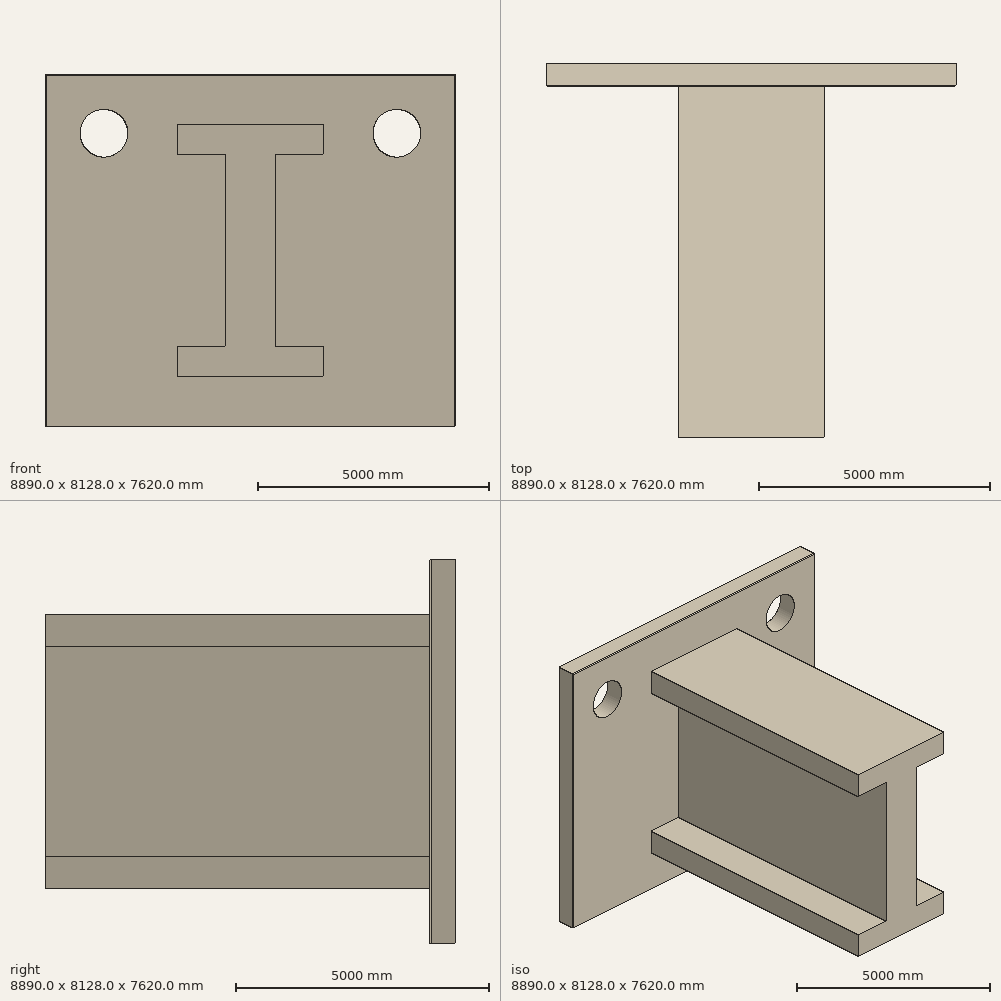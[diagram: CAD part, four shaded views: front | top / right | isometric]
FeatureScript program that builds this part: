
annotation { "Feature Type Name" : "Feature", "Feature Type Description" : "" }
export const myFeature = defineFeature(function(context is Context, id is Id, definition is map)
    precondition{}
    {
        {
            var Q0;
            Q0=qCreatedBy(makeId("Front.planeOp"),FACE);
            var sketch = newSketch(context, id + "F0", { "sketchPlane" : qUnion([Q0])});
            skLineSegment(sketch, "E0.bottom", {"start": v(-4445, 3810) * mm, "end": v(4445, 3810) * mm});
            skLineSegment(sketch, "E0.top", {"start": v(-4445, -3810) * mm, "end": v(4445, -3810) * mm});
            skLineSegment(sketch, "E0.left", {"start": v(-4445, 3810) * mm, "end": v(-4445, -3810) * mm});
            skLineSegment(sketch, "E0.right", {"start": v(4445, 3810) * mm, "end": v(4445, -3810) * mm});
            skPoint(sketch, "E0.middle", {"position": v(0, 0) * mm});
            skCircle(sketch, "E1", {"center": v(-3175, 2540) * mm, "radius": 517.04 * mm});
            skLineSegment(sketch, "E2", {"start": v(0, 3810) * mm, "end": v(0, -3810) * mm, "construction": true});
            skCircle(sketch, "E3.MirrorC", {"center": v(3175, 2540) * mm, "radius": 517.04 * mm});
            skSolve(sketch);
        }
        {
            var Q0;
            Q0=makeQuery(id+"F0.imprint","IMPRINT",FACE,{"disambiguationData":[TD([[makeQuery(id+"F0.imprint","IMPRINT",EDGE,{"derivedFrom":sQuery(id+"F0.wireOp",EDGE,"E0.bottom")}),-1.0]])]});
            extrude(context, id + "F1", {"entities" : qUnion([Q0]), "endBound" : BoundingType.SYMMETRIC, "depth" : 508 * mm});
        }
        {
            var Q0;
            Q0=makeQuery(id+"F1.opExtrude","CAP_FACE",FACE,{"disambiguationData":[OSD([sQuery(id+"F0.wireOp",EDGE,"E0.bottom"),sQuery(id+"F0.wireOp",EDGE,"E0.top"),sQuery(id+"F0.wireOp",EDGE,"E0.left"),sQuery(id+"F0.wireOp",EDGE,"E0.right"),sQuery(id+"F0.wireOp",EDGE,"E1"),sQuery(id+"F0.wireOp",EDGE,"E3.MirrorC")])],"isStart":false});
            var sketch = newSketch(context, id + "F2", { "sketchPlane" : qUnion([Q0])});
            skLineSegment(sketch, "E4", {"start": v(-1573.86, 2722.27) * mm, "end": v(0, 2722.27) * mm});
            skLineSegment(sketch, "E5", {"start": v(-1573.86, 2722.27) * mm, "end": v(-1573.86, 2076.57) * mm});
            skLineSegment(sketch, "E6", {"start": v(-1573.86, 2076.57) * mm, "end": v(-551.92, 2076.57) * mm});
            skLineSegment(sketch, "E7", {"start": v(-551.92, 2076.57) * mm, "end": v(-551.92, 0) * mm});
            skLineSegment(sketch, "E8", {"start": v(0, 0) * mm, "end": v(0, 2722.27) * mm, "construction": true});
            skLineSegment(sketch, "E9.MirrorCS", {"start": v(1573.86, 2722.27) * mm, "end": v(0, 2722.27) * mm});
            skLineSegment(sketch, "E10.MirrorCS", {"start": v(1573.86, 2722.27) * mm, "end": v(1573.86, 2076.57) * mm});
            skLineSegment(sketch, "E11.MirrorCS", {"start": v(1573.86, 2076.57) * mm, "end": v(551.92, 2076.57) * mm});
            skLineSegment(sketch, "E12.MirrorCS", {"start": v(551.92, 2076.57) * mm, "end": v(551.92, 0) * mm});
            skLineSegment(sketch, "E13", {"start": v(-551.92, 0) * mm, "end": v(0, 0) * mm, "construction": true});
            skLineSegment(sketch, "E14.MirrorCS", {"start": v(551.92, -2076.57) * mm, "end": v(551.92, 0) * mm});
            skLineSegment(sketch, "E15.MirrorCS", {"start": v(1573.86, -2076.57) * mm, "end": v(551.92, -2076.57) * mm});
            skLineSegment(sketch, "E16.MirrorCS", {"start": v(1573.86, -2722.27) * mm, "end": v(1573.86, -2076.57) * mm});
            skLineSegment(sketch, "E17.MirrorCS", {"start": v(1573.86, -2722.27) * mm, "end": v(0, -2722.27) * mm});
            skLineSegment(sketch, "E18.MirrorCS", {"start": v(-1573.86, -2722.27) * mm, "end": v(0, -2722.27) * mm});
            skLineSegment(sketch, "E19.MirrorCS", {"start": v(-1573.86, -2722.27) * mm, "end": v(-1573.86, -2076.57) * mm});
            skLineSegment(sketch, "E20.MirrorCS", {"start": v(-1573.86, -2076.57) * mm, "end": v(-551.92, -2076.57) * mm});
            skLineSegment(sketch, "E21.MirrorCS", {"start": v(-551.92, -2076.57) * mm, "end": v(-551.92, 0) * mm});
            skSolve(sketch);
        }
        {
            var Q0;
            Q0 = qSketchRegion(id + "F2", true);
            extrude(context, id + "F3", {"entities" : qUnion([Q0]), "operationType" : NewBodyOperationType.ADD, "depth" : 7620 * mm});
        }
        {
            var Q0;
            Q0=makeQuery(id+"F1.opExtrude","CAP_EDGE",EDGE,{"disambiguationData":[OSD([sQuery(id+"F0.wireOp",EDGE,"E0.bottom")])],"isStart":false});
            var Q1;
            Q1=makeQuery(id+"F1.opExtrude","CAP_EDGE",EDGE,{"disambiguationData":[OSD([sQuery(id+"F0.wireOp",EDGE,"E0.left")])],"isStart":false});
            var Q2;
            Q2=makeQuery(id+"F1.opExtrude","CAP_EDGE",EDGE,{"disambiguationData":[OSD([sQuery(id+"F0.wireOp",EDGE,"E0.right")])],"isStart":false});
            chamfer(context, id + "F4", {"entities" : qUnion([Q0, Q1, Q2]), "width" : 25.4 * mm, "tangentPropagation" : true});
        }
    });
